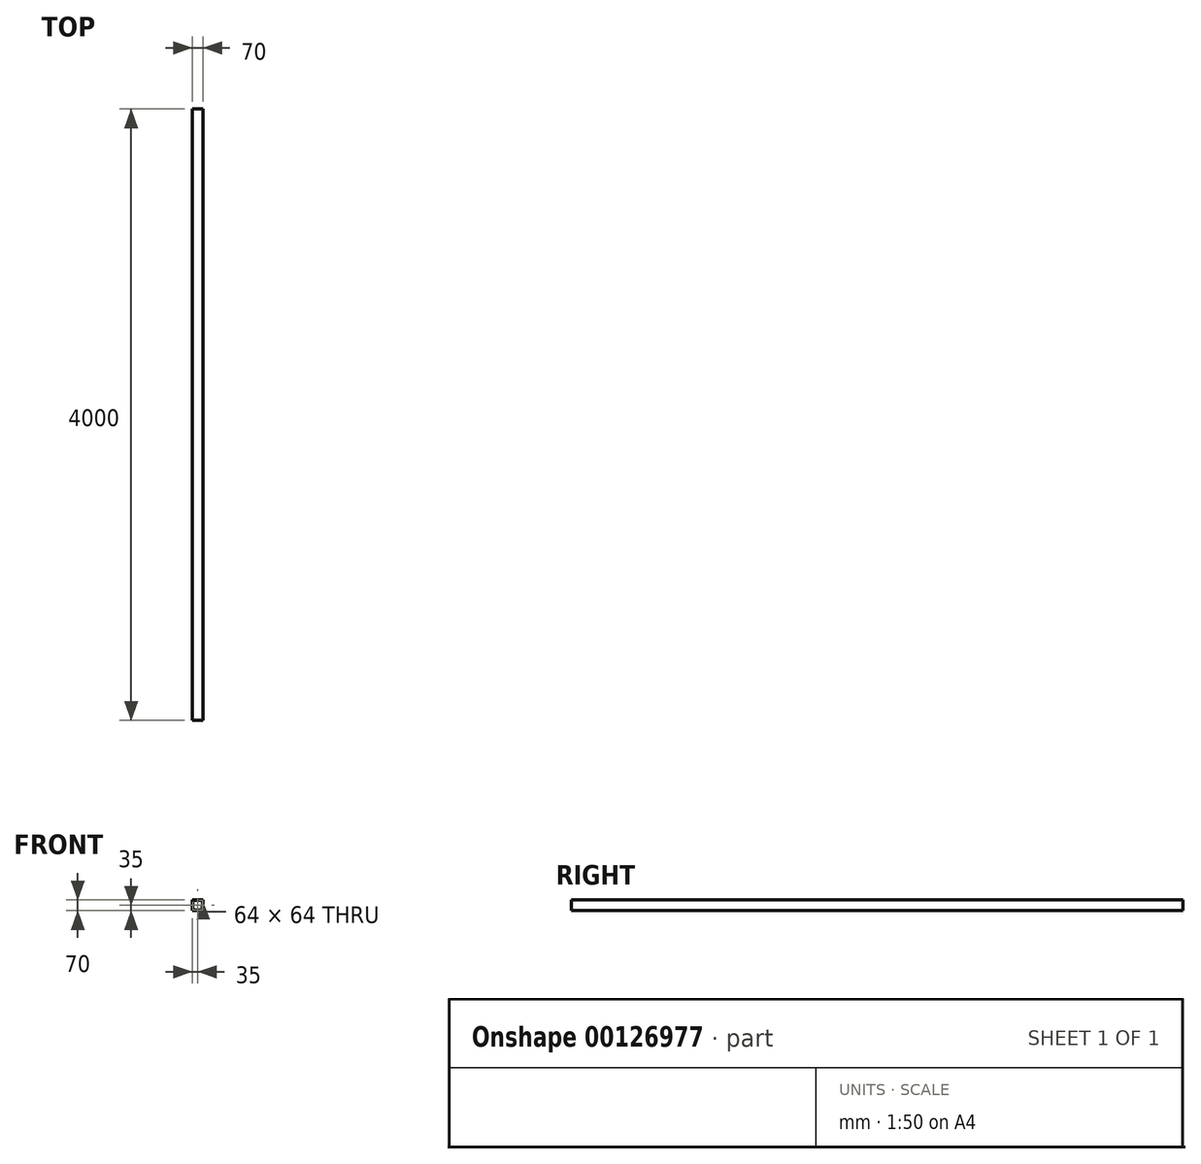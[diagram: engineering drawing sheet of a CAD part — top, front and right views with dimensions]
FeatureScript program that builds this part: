
annotation { "Feature Type Name" : "Feature", "Feature Type Description" : "" }
export const myFeature = defineFeature(function(context is Context, id is Id, definition is map)
    precondition{}
    {
        {
            var Q0;
            Q0=qCreatedBy(makeId("Front.planeOp"),FACE);
            var sketch = newSketch(context, id + "F0", { "sketchPlane" : qUnion([Q0])});
            skLineSegment(sketch, "E0.bottom", {"start": v(35, 35) * mm, "end": v(-35, 35) * mm});
            skLineSegment(sketch, "E0.top", {"start": v(35, -35) * mm, "end": v(-35, -35) * mm});
            skLineSegment(sketch, "E0.left", {"start": v(35, 35) * mm, "end": v(35, -35) * mm});
            skLineSegment(sketch, "E0.right", {"start": v(-35, 35) * mm, "end": v(-35, -35) * mm});
            skPoint(sketch, "E0.middle", {"position": v(0, 0) * mm});
            skLineSegment(sketch, "E1.bottom", {"start": v(32, 32) * mm, "end": v(-32, 32) * mm});
            skLineSegment(sketch, "E1.top", {"start": v(32, -32) * mm, "end": v(-32, -32) * mm});
            skLineSegment(sketch, "E1.left", {"start": v(32, 32) * mm, "end": v(32, -32) * mm});
            skLineSegment(sketch, "E1.right", {"start": v(-32, 32) * mm, "end": v(-32, -32) * mm});
            skSolve(sketch);
        }
        {
            var Q0;
            Q0=makeQuery(id+"F0.imprint","IMPRINT",FACE,{"disambiguationData":[TD([[makeQuery(id+"F0.imprint","IMPRINT",EDGE,{"derivedFrom":sQuery(id+"F0.wireOp",EDGE,"E0.bottom")}),1.0]])]});
            extrude(context, id + "F1", {"entities" : qUnion([Q0]), "depth" : 4000 * mm});
        }
    });
